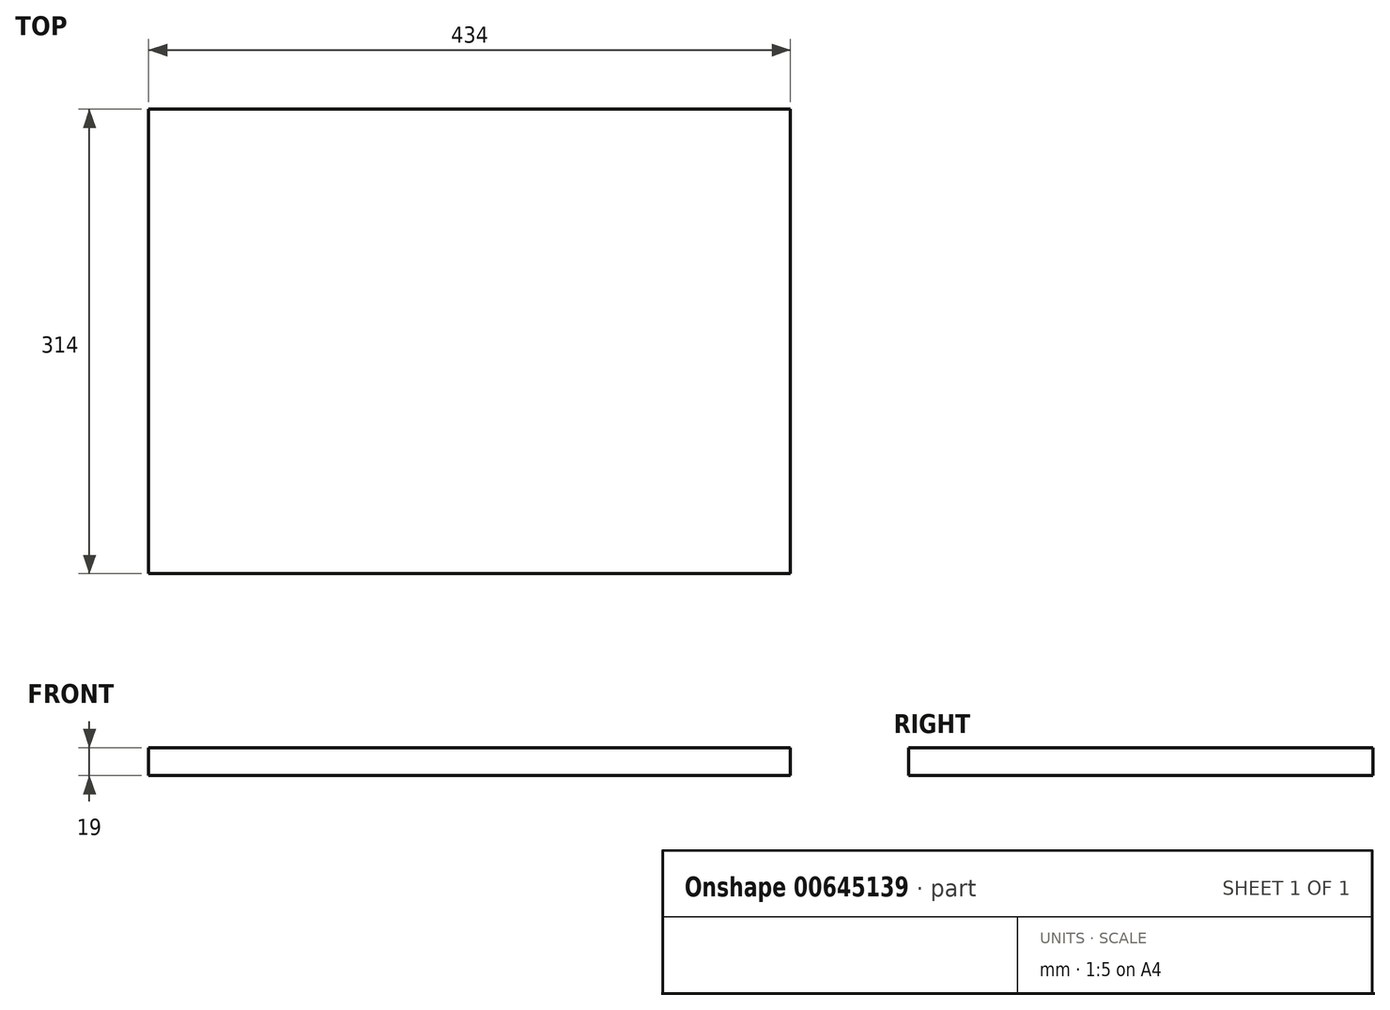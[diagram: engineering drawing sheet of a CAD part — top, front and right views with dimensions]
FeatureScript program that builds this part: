
annotation { "Feature Type Name" : "Feature", "Feature Type Description" : "" }
export const myFeature = defineFeature(function(context is Context, id is Id, definition is map)
    precondition{}
    {
        {
            var Q0;
            Q0=qCreatedBy(makeId("Top.planeOp"),FACE);
            var sketch = newSketch(context, id + "F0", { "sketchPlane" : qUnion([Q0])});
            skLineSegment(sketch, "E0.bottom", {"start": v(217, -157) * mm, "end": v(-217, -157) * mm});
            skLineSegment(sketch, "E0.top", {"start": v(217, 157) * mm, "end": v(-217, 157) * mm});
            skLineSegment(sketch, "E0.left", {"start": v(217, -157) * mm, "end": v(217, 157) * mm});
            skLineSegment(sketch, "E0.right", {"start": v(-217, -157) * mm, "end": v(-217, 157) * mm});
            skPoint(sketch, "E0.middle", {"position": v(0, 0) * mm});
            skSolve(sketch);
        }
        {
            var Q0;
            Q0 = qSketchRegion(id + "F0", true);
            extrude(context, id + "F1", {"entities" : qUnion([Q0]), "depth" : 19 * mm, "offsetDistance" : 25.4 * mm});
        }
    });
